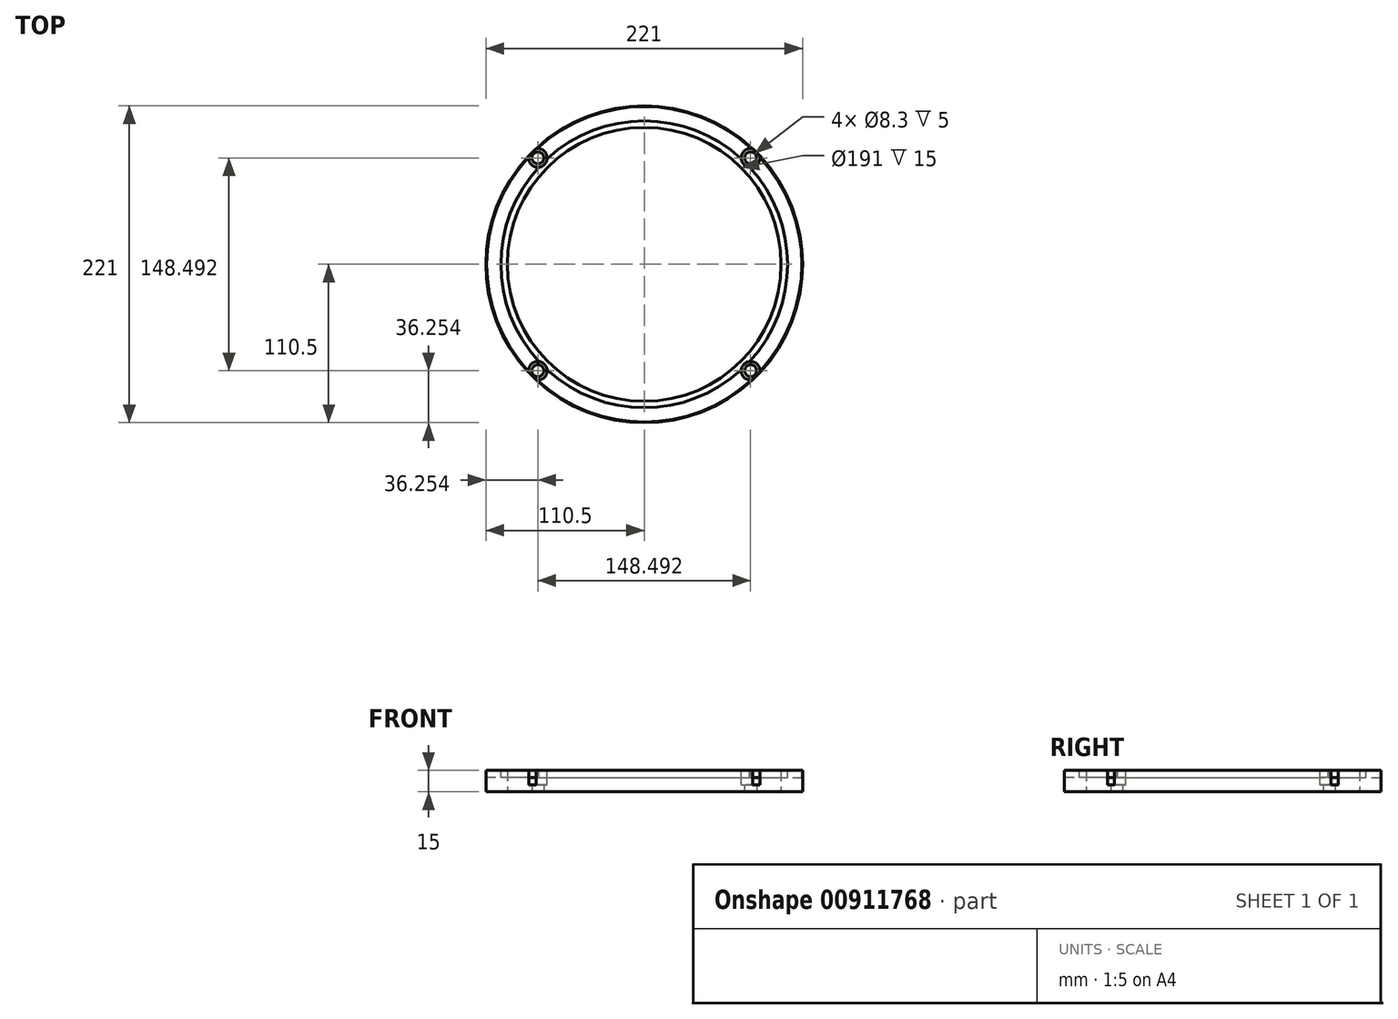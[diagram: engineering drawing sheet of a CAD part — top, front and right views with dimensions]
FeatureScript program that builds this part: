
annotation { "Feature Type Name" : "Feature", "Feature Type Description" : "" }
export const myFeature = defineFeature(function(context is Context, id is Id, definition is map)
    precondition{}
    {
        {
            var Q0;
            Q0=qCreatedBy(makeId("Top.planeOp"),FACE);
            var sketch = newSketch(context, id + "F0", { "sketchPlane" : qUnion([Q0])});
            skCircle(sketch, "E0", {"center": v(0, 0) * mm, "radius": 110.5 * mm});
            skCircle(sketch, "E1", {"center": v(0, 0) * mm, "radius": 95.5 * mm});
            skSolve(sketch);
        }
        {
            var Q0;
            Q0=qSketchRegion(id+"F0",true);
            extrude(context, id + "F1", {"entities" : qUnion([Q0]), "depth" : 15 * mm, "offsetDistance" : 25 * mm});
        }
        {
            var Q0;
            Q0=makeQuery(id+"F1.opExtrude","CAP_FACE",FACE,{"disambiguationData":[OSD([sQuery(id+"F0.wireOp",EDGE,"E0"),sQuery(id+"F0.wireOp",EDGE,"E1")])],"isStart":false});
            var sketch = newSketch(context, id + "F2", { "sketchPlane" : qUnion([Q0])});
            skCircle(sketch, "E2", {"center": v(0, 0) * mm, "radius": 110 * mm});
            skCircle(sketch, "E3", {"center": v(0, 0) * mm, "radius": 100 * mm});
            skSolve(sketch);
        }
        {
            var Q0;
            Q0=qSketchRegion(id+"F2",true);
            extrude(context, id + "F3", {"entities" : qUnion([Q0]), "operationType" : NewBodyOperationType.REMOVE, "oppositeDirection" : true, "depth" : 5 * mm, "offsetDistance" : 25 * mm});
        }
        {
            var Q0;
            Q0=makeQuery(id+"F1.opExtrude","CAP_FACE",FACE,{"disambiguationData":[OSD([sQuery(id+"F0.wireOp",EDGE,"E0"),sQuery(id+"F0.wireOp",EDGE,"E1")])],"isStart":true});
            var sketch = newSketch(context, id + "F4", { "sketchPlane" : qUnion([Q0])});
            skPoint(sketch, "E4", {"position": v(-74.25, 74.25) * mm});
            skPoint(sketch, "E5", {"position": v(-74.25, -74.25) * mm});
            skPoint(sketch, "E6", {"position": v(74.25, 74.25) * mm});
            skPoint(sketch, "E7", {"position": v(74.25, -74.25) * mm});
            skCircle(sketch, "E8", {"center": v(-74.25, 74.25) * mm, "radius": 4.15 * mm});
            skCircle(sketch, "E9", {"center": v(-74.25, -74.25) * mm, "radius": 4.15 * mm});
            skCircle(sketch, "E10", {"center": v(74.25, 74.25) * mm, "radius": 4.15 * mm});
            skCircle(sketch, "E11", {"center": v(74.25, -74.25) * mm, "radius": 4.15 * mm});
            skSolve(sketch);
        }
        {
            var Q0;
            Q0=qSketchRegion(id+"F4",true);
            extrude(context, id + "F5", {"entities" : qUnion([Q0]), "operationType" : NewBodyOperationType.REMOVE, "oppositeDirection" : true, "depth" : 25 * mm, "offsetDistance" : 25 * mm});
        }
        {
            var Q0;
            {var subQ0=sQuery(id+"F0.wireOp",EDGE,"E1");Q0=makeQuery(id+"F3.boolean.opBoolean","SPLIT",FACE,{"disambiguationData":[TD([makeQuery(id+"F1.opExtrude","SWEPT_FACE",FACE,{"disambiguationData":[OSD([subQ0])]})])],"derivedFrom":makeQuery(id+"F1.opExtrude","CAP_FACE",FACE,{"disambiguationData":[OSD([sQuery(id+"F0.wireOp",EDGE,"E0"),subQ0])],"isStart":false})});}
            var sketch = newSketch(context, id + "F6", { "sketchPlane" : qUnion([Q0])});
            skPoint(sketch, "E12", {"position": v(-74.25, 74.25) * mm});
            skPoint(sketch, "E13", {"position": v(-74.25, -74.25) * mm});
            skPoint(sketch, "E14", {"position": v(74.25, 74.25) * mm});
            skPoint(sketch, "E15", {"position": v(74.25, -74.25) * mm});
            skCircle(sketch, "E16", {"center": v(-74.25, 74.25) * mm, "radius": 6.5 * mm});
            skCircle(sketch, "E17", {"center": v(74.25, 74.25) * mm, "radius": 6.5 * mm});
            skCircle(sketch, "E18", {"center": v(74.25, -74.25) * mm, "radius": 6.5 * mm});
            skCircle(sketch, "E19", {"center": v(-74.25, -74.25) * mm, "radius": 6.5 * mm});
            skSolve(sketch);
        }
        {
            var Q0;
            Q0=qSketchRegion(id+"F6",true);
            extrude(context, id + "F7", {"entities" : qUnion([Q0]), "operationType" : NewBodyOperationType.REMOVE, "oppositeDirection" : true, "depth" : 10 * mm, "offsetDistance" : 25 * mm});
        }
    });
